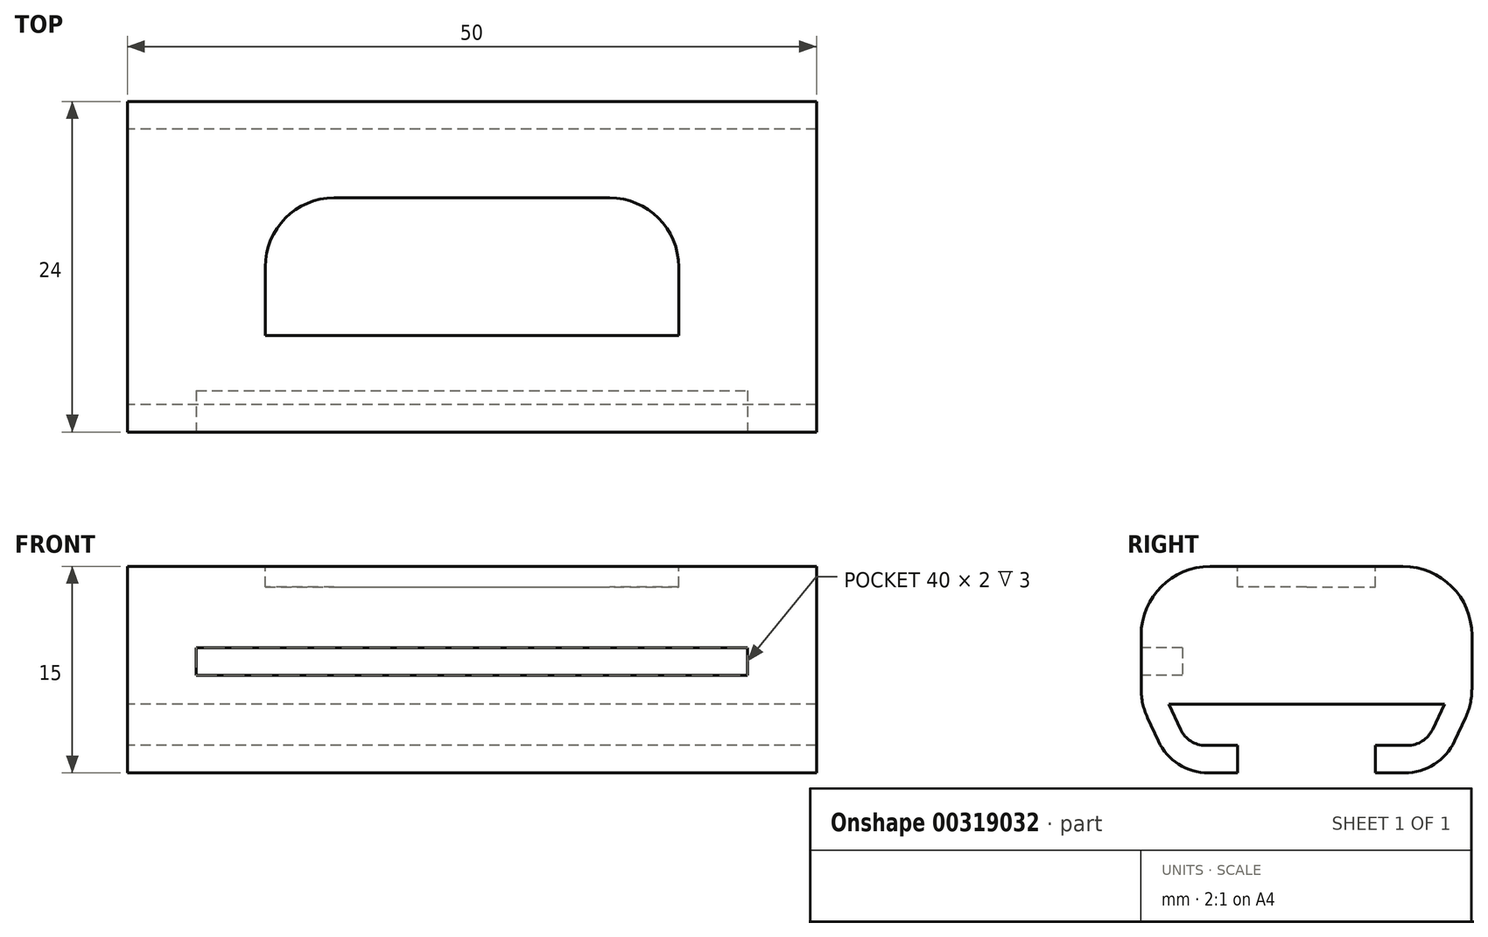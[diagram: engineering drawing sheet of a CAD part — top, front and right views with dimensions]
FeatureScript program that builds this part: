
annotation { "Feature Type Name" : "Feature", "Feature Type Description" : "" }
export const myFeature = defineFeature(function(context is Context, id is Id, definition is map)
    precondition{}
    {
        {
            var Q0;
            Q0=qCreatedBy(makeId("Top.planeOp"),FACE);
            var sketch = newSketch(context, id + "F0", { "sketchPlane" : qUnion([Q0])});
            skLineSegment(sketch, "E0.bottom", {"start": v(-25, 12) * mm, "end": v(25, 12) * mm});
            skLineSegment(sketch, "E0.top", {"start": v(-25, -12) * mm, "end": v(25, -12) * mm});
            skLineSegment(sketch, "E0.left", {"start": v(-25, 12) * mm, "end": v(-25, -12) * mm});
            skLineSegment(sketch, "E0.right", {"start": v(25, 12) * mm, "end": v(25, -12) * mm});
            skPoint(sketch, "E0.middle", {"position": v(0, 0) * mm});
            skSolve(sketch);
        }
        {
            var Q0;
            Q0=makeQuery(id+"F0.imprint","IMPRINT",FACE,{"disambiguationData":[TD([[makeQuery(id+"F0.imprint","IMPRINT",EDGE,{"derivedFrom":sQuery(id+"F0.wireOp",EDGE,"E0.bottom")}),-1.0]])]});
            extrude(context, id + "F1", {"entities" : qUnion([Q0]), "depth" : 10 * mm});
        }
        {
            var Q0;
            Q0=makeQuery(id+"F1.opExtrude","SWEPT_FACE",FACE,{"disambiguationData":[OSD([sQuery(id+"F0.wireOp",EDGE,"E0.left")])]});
            var sketch = newSketch(context, id + "F2", { "sketchPlane" : qUnion([Q0])});
            skLineSegment(sketch, "E1", {"start": v(-12, 0) * mm, "end": v(-9.67, -5) * mm});
            skLineSegment(sketch, "E2", {"start": v(-9.67, -5) * mm, "end": v(-5, -5) * mm});
            skLineSegment(sketch, "E3", {"start": v(-5, -5) * mm, "end": v(-5, -3) * mm});
            skLineSegment(sketch, "E4", {"start": v(-5, -3) * mm, "end": v(-8.6, -3) * mm});
            skLineSegment(sketch, "E5", {"start": v(-8.6, -3) * mm, "end": v(-10, 0) * mm});
            skLineSegment(sketch, "E6", {"start": v(-10, 0) * mm, "end": v(-12, 0) * mm});
            skLineSegment(sketch, "E7.MirrorCS", {"start": v(10, 0) * mm, "end": v(12, 0) * mm});
            skLineSegment(sketch, "E8.MirrorCS", {"start": v(8.6, -3) * mm, "end": v(10, 0) * mm});
            skLineSegment(sketch, "E9.MirrorCS", {"start": v(5, -3) * mm, "end": v(8.6, -3) * mm});
            skLineSegment(sketch, "E10.MirrorCS", {"start": v(12, 0) * mm, "end": v(9.67, -5) * mm});
            skLineSegment(sketch, "E11.MirrorCS", {"start": v(5, -5) * mm, "end": v(5, -3) * mm});
            skLineSegment(sketch, "E12.MirrorCS", {"start": v(9.67, -5) * mm, "end": v(5, -5) * mm});
            skSolve(sketch);
        }
        {
            var Q0;
            Q0 = qSketchRegion(id + "F2", true);
            var Q1;
            Q1=makeQuery(id+"F1.opExtrude","SWEPT_FACE",FACE,{"disambiguationData":[OSD([sQuery(id+"F0.wireOp",EDGE,"E0.right")])]});
            extrude(context, id + "F3", {"entities" : qUnion([Q0]), "operationType" : NewBodyOperationType.ADD, "endBound" : BoundingType.UP_TO_SURFACE, "oppositeDirection" : true, "endBoundEntityFace" : qUnion([Q1]), "depth" : 50 * mm});
        }
        {
            var Q0;
            Q0=makeQuery(id+"F1.opExtrude","CAP_EDGE",EDGE,{"disambiguationData":[OSD([sQuery(id+"F0.wireOp",EDGE,"E0.bottom")])],"isStart":false});
            var Q1;
            Q1=makeQuery(id+"F1.opExtrude","CAP_EDGE",EDGE,{"disambiguationData":[OSD([sQuery(id+"F0.wireOp",EDGE,"E0.top")])],"isStart":false});
            var Q2;
            {var subQ0=sQuery(id+"F0.wireOp",EDGE,"E0.bottom");Q2=makeQuery(id+"F3.boolean.opBoolean","MERGE",EDGE,{"derivedFrom":[makeQuery(id+"F1.opExtrude","CAP_EDGE",EDGE,{"disambiguationData":[OSD([subQ0])],"isStart":true}),makeQuery(id+"F3.opExtrude","SWEPT_EDGE",EDGE,{"disambiguationData":[OSD([subQ0,sQuery(id+"F0.wireOp",EDGE,"E0.left"),sQuery(id+"F2.wireOp",EDGE,"E1"),sQuery(id+"F2.wireOp",EDGE,"E6")])]})]});}
            var Q3;
            {var subQ0=sQuery(id+"F0.wireOp",EDGE,"E0.top");Q3=makeQuery(id+"F3.boolean.opBoolean","MERGE",EDGE,{"derivedFrom":[makeQuery(id+"F1.opExtrude","CAP_EDGE",EDGE,{"disambiguationData":[OSD([subQ0])],"isStart":true}),makeQuery(id+"F3.opExtrude","SWEPT_EDGE",EDGE,{"disambiguationData":[OSD([subQ0,sQuery(id+"F0.wireOp",EDGE,"E0.left"),sQuery(id+"F2.wireOp",EDGE,"E7.MirrorCS"),sQuery(id+"F2.wireOp",EDGE,"E10.MirrorCS")])]})]});}
            fillet(context, id + "F4", {"entities" : qUnion([Q0, Q1, Q2, Q3]), "radius" : 5 * mm, "tangentPropagation" : true, "allowEdgeOverflow" : false});
        }
        {
            var Q0;
            Q0=makeQuery(id+"F3.opExtrude","SWEPT_EDGE",EDGE,{"disambiguationData":[OSD([sQuery(id+"F2.wireOp",EDGE,"E4"),sQuery(id+"F2.wireOp",EDGE,"E5")])]});
            var Q1;
            Q1=makeQuery(id+"F3.opExtrude","SWEPT_EDGE",EDGE,{"disambiguationData":[OSD([sQuery(id+"F2.wireOp",EDGE,"E8.MirrorCS"),sQuery(id+"F2.wireOp",EDGE,"E9.MirrorCS")])]});
            fillet(context, id + "F5", {"entities" : qUnion([Q0, Q1]), "radius" : 2 * mm, "tangentPropagation" : true, "allowEdgeOverflow" : false});
        }
        {
            var Q0;
            Q0=makeQuery(id+"F3.opExtrude","SWEPT_EDGE",EDGE,{"disambiguationData":[OSD([sQuery(id+"F2.wireOp",EDGE,"E1"),sQuery(id+"F2.wireOp",EDGE,"E2")])]});
            var Q1;
            Q1=makeQuery(id+"F3.opExtrude","SWEPT_EDGE",EDGE,{"disambiguationData":[OSD([sQuery(id+"F2.wireOp",EDGE,"E10.MirrorCS"),sQuery(id+"F2.wireOp",EDGE,"E12.MirrorCS")])]});
            fillet(context, id + "F6", {"entities" : qUnion([Q0, Q1]), "radius" : 4 * mm, "tangentPropagation" : true, "allowEdgeOverflow" : false});
        }
        {
            var Q0;
            Q0=makeQuery(id+"F1.opExtrude","SWEPT_FACE",FACE,{"disambiguationData":[OSD([sQuery(id+"F0.wireOp",EDGE,"E0.top")])]});
            var sketch = newSketch(context, id + "F7", { "sketchPlane" : qUnion([Q0])});
            skLineSegment(sketch, "E13.bottom", {"start": v(-20, 4.09) * mm, "end": v(20, 4.09) * mm});
            skLineSegment(sketch, "E13.top", {"start": v(-20, 2.09) * mm, "end": v(20, 2.09) * mm});
            skLineSegment(sketch, "E13.left", {"start": v(-20, 4.09) * mm, "end": v(-20, 2.09) * mm});
            skLineSegment(sketch, "E13.right", {"start": v(20, 4.09) * mm, "end": v(20, 2.09) * mm});
            skPoint(sketch, "E13.middle", {"position": v(0, 3.09) * mm});
            skPoint(sketch, "E13.middle.positionSnap0", {"position": v(0, 1.1) * mm});
            skPoint(sketch, "E13.centerSnap0", {"position": v(0, 1.1) * mm});
            skSolve(sketch);
        }
        {
            var Q0;
            Q0=makeQuery(id+"F7.imprint","IMPRINT",FACE,{"disambiguationData":[TD([[makeQuery(id+"F7.imprint","IMPRINT",EDGE,{"derivedFrom":sQuery(id+"F7.wireOp",EDGE,"E13.bottom")}),-1.0]])]});
            extrude(context, id + "F8", {"entities" : qUnion([Q0]), "operationType" : NewBodyOperationType.REMOVE, "oppositeDirection" : true, "depth" : 3 * mm});
        }
        {
            var Q0;
            Q0=makeQuery(id+"F1.opExtrude","CAP_FACE",FACE,{"disambiguationData":[OSD([sQuery(id+"F0.wireOp",EDGE,"E0.bottom"),sQuery(id+"F0.wireOp",EDGE,"E0.top"),sQuery(id+"F0.wireOp",EDGE,"E0.left"),sQuery(id+"F0.wireOp",EDGE,"E0.right")])],"isStart":false});
            var sketch = newSketch(context, id + "F9", { "sketchPlane" : qUnion([Q0])});
            skLineSegment(sketch, "E14.bottom", {"start": v(-15, 5) * mm, "end": v(15, 5) * mm});
            skLineSegment(sketch, "E14.top", {"start": v(-15, -5) * mm, "end": v(15, -5) * mm});
            skLineSegment(sketch, "E14.left", {"start": v(-15, 5) * mm, "end": v(-15, -5) * mm});
            skLineSegment(sketch, "E14.right", {"start": v(15, 5) * mm, "end": v(15, -5) * mm});
            skPoint(sketch, "E14.middle", {"position": v(0, 0) * mm});
            skSolve(sketch);
        }
        {
            var Q0;
            Q0 = qSketchRegion(id + "F9", true);
            extrude(context, id + "F10", {"entities" : qUnion([Q0]), "operationType" : NewBodyOperationType.REMOVE, "oppositeDirection" : true, "depth" : 1.5 * mm});
        }
        {
            var Q0;
            Q0=makeQuery(id+"F10.boolean.opBoolean","COPY",EDGE,{"derivedFrom":makeQuery(id+"F10.opExtrude","SWEPT_EDGE",EDGE,{"disambiguationData":[OSD([sQuery(id+"F9.wireOp",EDGE,"E14.bottom"),sQuery(id+"F9.wireOp",EDGE,"E14.left")])]})});
            var Q1;
            Q1=makeQuery(id+"F10.boolean.opBoolean","COPY",EDGE,{"derivedFrom":makeQuery(id+"F10.opExtrude","SWEPT_EDGE",EDGE,{"disambiguationData":[OSD([sQuery(id+"F9.wireOp",EDGE,"E14.bottom"),sQuery(id+"F9.wireOp",EDGE,"E14.right")])]})});
            fillet(context, id + "F11", {"entities" : qUnion([Q0, Q1]), "radius" : 5 * mm, "tangentPropagation" : true, "allowEdgeOverflow" : false});
        }
    });
